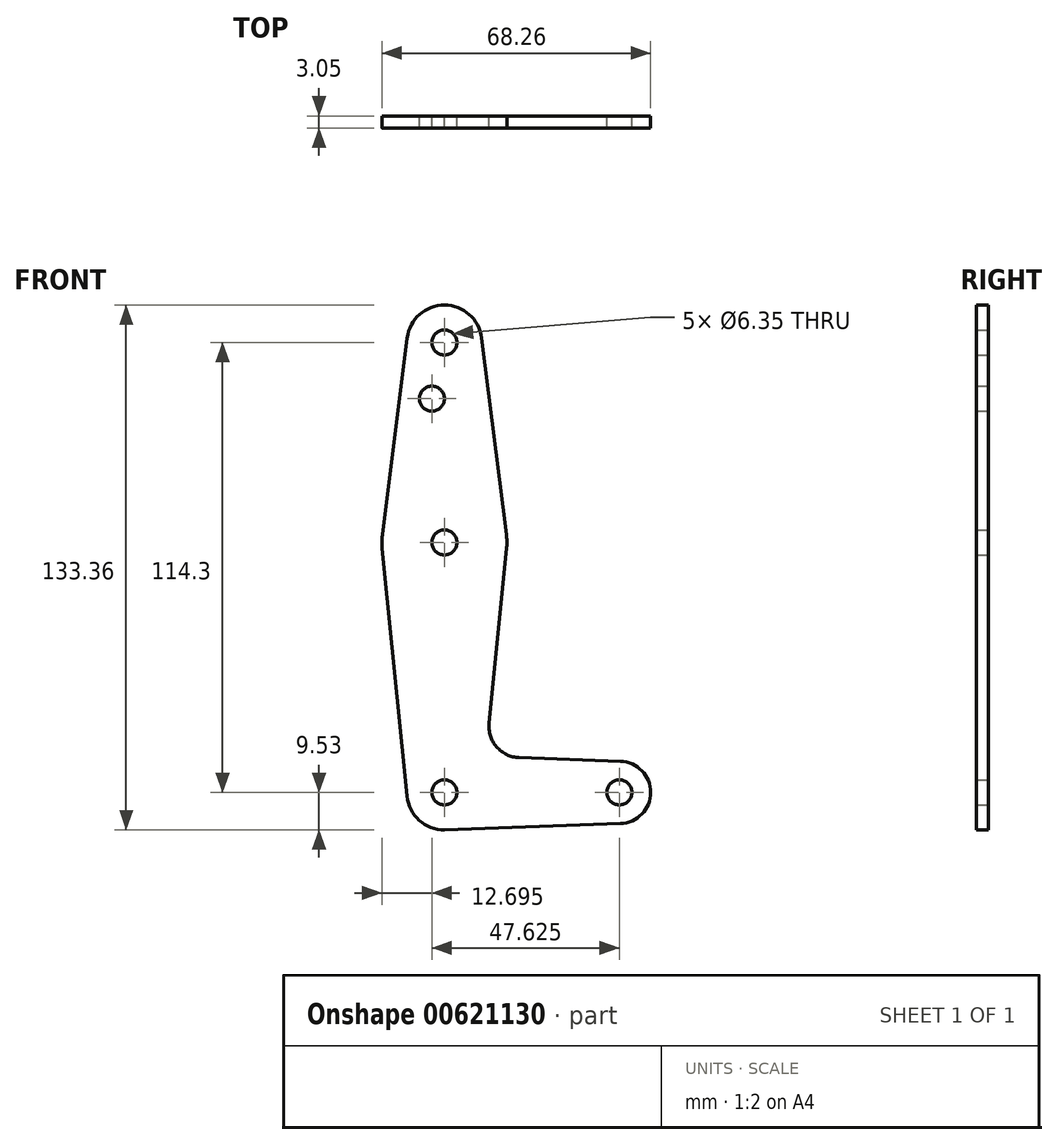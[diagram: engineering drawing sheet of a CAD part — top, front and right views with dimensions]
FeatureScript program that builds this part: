
annotation { "Feature Type Name" : "Feature", "Feature Type Description" : "" }
export const myFeature = defineFeature(function(context is Context, id is Id, definition is map)
    precondition{}
    {
        {
            var Q0;
            Q0=qCreatedBy(makeId("Front.planeOp"),FACE);
            var sketch = newSketch(context, id + "F0", { "sketchPlane" : qUnion([Q0])});
            skLineSegment(sketch, "E0", {"start": v(0, 0) * mm, "end": v(0, 114.3) * mm, "construction": true});
            skLineSegment(sketch, "E1", {"start": v(0, 0) * mm, "end": v(44.45, 0) * mm, "construction": true});
            skCircle(sketch, "E2", {"center": v(0, 0) * mm, "radius": 9.53 * mm});
            skCircle(sketch, "E3", {"center": v(44.45, 0) * mm, "radius": 7.94 * mm});
            skCircle(sketch, "E4", {"center": v(0, 114.3) * mm, "radius": 9.53 * mm});
            skCircle(sketch, "E5", {"center": v(0, 63.5) * mm, "radius": 15.88 * mm});
            skLineSegment(sketch, "E6", {"start": v(0, -9.53) * mm, "end": v(44.73, -7.93) * mm});
            skLineSegment(sketch, "E7", {"start": v(-9.45, 115.5) * mm, "end": v(-15.75, 65.48) * mm});
            skLineSegment(sketch, "E8", {"start": v(18.97, 8.85) * mm, "end": v(44.73, 7.93) * mm});
            skLineSegment(sketch, "E9", {"start": v(-9.48, -0.95) * mm, "end": v(-15.8, 61.91) * mm});
            skLineSegment(sketch, "E10.MirrorCS", {"start": v(9.45, 115.5) * mm, "end": v(15.75, 65.48) * mm});
            skLineSegment(sketch, "E11.MirrorCS", {"start": v(11.34, 17.59) * mm, "end": v(15.8, 61.91) * mm});
            skCircle(sketch, "E12", {"center": v(0, 114.3) * mm, "radius": 3.18 * mm});
            skCircle(sketch, "E13", {"center": v(0, 63.5) * mm, "radius": 3.18 * mm});
            skCircle(sketch, "E14", {"center": v(0, 0) * mm, "radius": 3.18 * mm});
            skCircle(sketch, "E15", {"center": v(44.45, 0) * mm, "radius": 3.18 * mm});
            skCircle(sketch, "E16", {"center": v(-3.18, 100.03) * mm, "radius": 3.18 * mm});
            skPoint(sketch, "E17.newPointA", {"position": v(9.48, -0.95) * mm});
            skPoint(sketch, "E17.newPointB", {"position": v(0, 9.53) * mm});
            skArc(sketch, "E17.filletArc", {"start": v(11.34, 17.59) * mm, "mid": v(13.26, 11.57) * mm, "end": v(18.97, 8.85) * mm});
            skSolve(sketch);
        }
        {
            var Q0;
            Q0=makeQuery(id+"F0.imprint","IMPRINT",FACE,{"disambiguationData":[TD([[makeQuery(id+"F0.imprint","IMPRINT",EDGE,{"derivedFrom":sQuery(id+"F0.wireOp",EDGE,"E12")}),-1.0]])]});
            var Q1;
            {var subQ0=sQuery(id+"F0.wireOp",EDGE,"E7");Q1=makeQuery(id+"F0.imprint","IMPRINT",FACE,{"disambiguationData":[TD([[makeQuery(id+"F0.imprint","IMPRINT",EDGE,{"derivedFrom":subQ0}),1.0]])]});}
            var Q2;
            {var subQ6=sQuery(id+"F0.wireOp",EDGE,"E8");Q2=makeQuery(id+"F0.imprint","IMPRINT",FACE,{"disambiguationData":[TD([[makeQuery(id+"F0.imprint","IMPRINT",EDGE,{"derivedFrom":subQ6}),-1.0]])]});}
            var Q3;
            Q3=makeQuery(id+"F0.imprint","IMPRINT",FACE,{"disambiguationData":[TD([[makeQuery(id+"F0.imprint","IMPRINT",EDGE,{"derivedFrom":sQuery(id+"F0.wireOp",EDGE,"E13")}),-1.0]])]});
            var Q4;
            Q4=makeQuery(id+"F0.imprint","IMPRINT",FACE,{"disambiguationData":[TD([[makeQuery(id+"F0.imprint","IMPRINT",EDGE,{"derivedFrom":sQuery(id+"F0.wireOp",EDGE,"E14")}),-1.0]])]});
            var Q5;
            Q5=makeQuery(id+"F0.imprint","IMPRINT",FACE,{"disambiguationData":[TD([[makeQuery(id+"F0.imprint","IMPRINT",EDGE,{"derivedFrom":sQuery(id+"F0.wireOp",EDGE,"E15")}),-1.0]])]});
            extrude(context, id + "F1", {"entities" : qUnion([Q0, Q1, Q2, Q3, Q4, Q5]), "depth" : 3.05 * mm, "offsetDistance" : 25.4 * mm});
        }
    });
